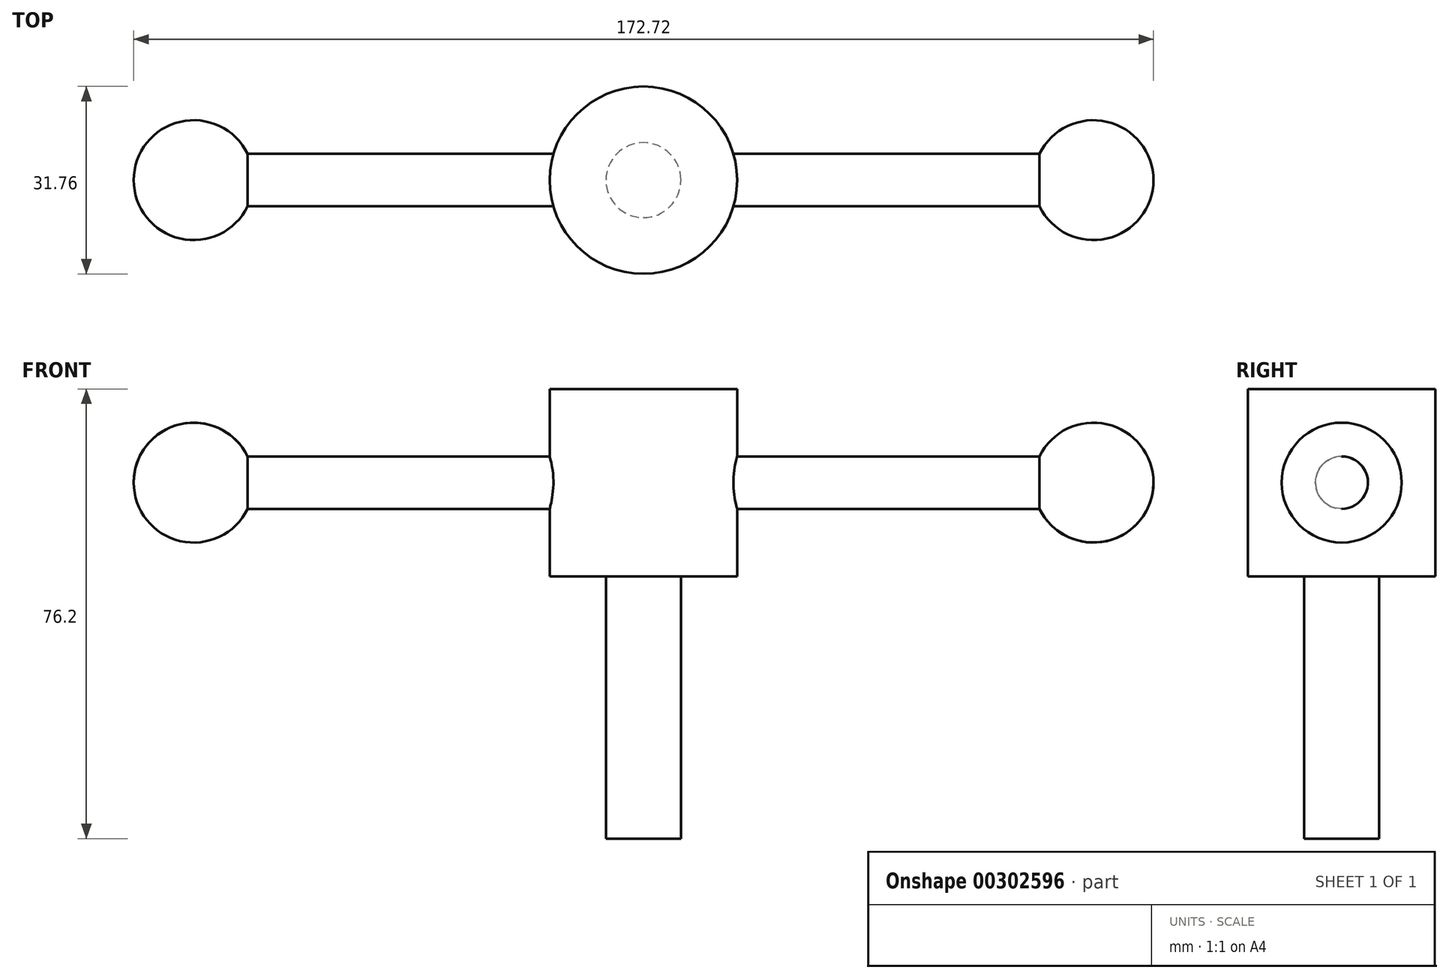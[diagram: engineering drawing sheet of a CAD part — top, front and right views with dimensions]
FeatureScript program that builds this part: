
annotation { "Feature Type Name" : "Feature", "Feature Type Description" : "" }
export const myFeature = defineFeature(function(context is Context, id is Id, definition is map)
    precondition{}
    {
        {
            var Q0;
            Q0=qCreatedBy(makeId("Top.planeOp"),FACE);
            var sketch = newSketch(context, id + "F0", { "sketchPlane" : qUnion([Q0])});
            skCircle(sketch, "E0", {"center": v(0, 0) * mm, "radius": 15.88 * mm});
            skCircle(sketch, "E1", {"center": v(0, 0) * mm, "radius": 6.35 * mm});
            skSolve(sketch);
        }
        {
            var Q0;
            Q0=makeQuery(id+"F0.imprint","IMPRINT",FACE,{"disambiguationData":[TD([[makeQuery(id+"F0.imprint","IMPRINT",EDGE,{"derivedFrom":sQuery(id+"F0.wireOp",EDGE,"E0")}),1.0]])]});
            var Q1;
            Q1=makeQuery(id+"F0.imprint","IMPRINT",FACE,{"disambiguationData":[TD([[makeQuery(id+"F0.imprint","IMPRINT",EDGE,{"derivedFrom":sQuery(id+"F0.wireOp",EDGE,"E1")}),1.0]])]});
            extrude(context, id + "F1", {"entities" : qUnion([Q0, Q1]), "depth" : 31.75 * mm});
        }
        {
            var Q0;
            Q0=makeQuery(id+"F0.imprint","IMPRINT",FACE,{"disambiguationData":[TD([[makeQuery(id+"F0.imprint","IMPRINT",EDGE,{"derivedFrom":sQuery(id+"F0.wireOp",EDGE,"E1")}),1.0]])]});
            extrude(context, id + "F2", {"entities" : qUnion([Q0]), "operationType" : NewBodyOperationType.ADD, "oppositeDirection" : true, "depth" : 44.45 * mm});
        }
        {
            var Q0;
            Q0=qCreatedBy(makeId("Right.planeOp"),FACE);
            var sketch = newSketch(context, id + "F3", { "sketchPlane" : qUnion([Q0])});
            skLineSegment(sketch, "E2", {"start": v(-15.88, 0) * mm, "end": v(-15.88, 31.75) * mm});
            skLineSegment(sketch, "E3", {"start": v(15.88, 31.75) * mm, "end": v(15.88, 0) * mm});
            skCircle(sketch, "E4", {"center": v(0, 15.88) * mm, "radius": 4.45 * mm});
            skSolve(sketch);
        }
        {
            var Q0;
            Q0 = qSketchRegion(id + "F3", true);
            extrude(context, id + "F4", {"entities" : qUnion([Q0]), "operationType" : NewBodyOperationType.ADD, "depth" : 139.7 * mm, "symmetric" : true});
        }
        {
            var Q0;
            Q0=qCreatedBy(makeId("Front.planeOp"),FACE);
            var sketch = newSketch(context, id + "F5", { "sketchPlane" : qUnion([Q0])});
            skArc(sketch, "E5", {"start": v(86.39, 15.88) * mm, "mid": v(76.23, 26.04) * mm, "end": v(66.07, 15.88) * mm});
            skLineSegment(sketch, "E6", {"start": v(15.88, 20.32) * mm, "end": v(66.1, 20.32) * mm});
            skLineSegment(sketch, "E7", {"start": v(66.04, 11.43) * mm, "end": v(15.88, 11.43) * mm});
            skLineSegment(sketch, "E8", {"start": v(76.23, 15.88) * mm, "end": v(66.07, 15.88) * mm});
            skLineSegment(sketch, "E9", {"start": v(66.04, 11.43) * mm, "end": v(66.1, 20.32) * mm});
            skArc(sketch, "E10", {"start": v(-66.01, 15.88) * mm, "mid": v(-76.17, 26.04) * mm, "end": v(-86.33, 15.87) * mm});
            skLineSegment(sketch, "E11", {"start": v(-76.17, 15.88) * mm, "end": v(-66.01, 15.88) * mm, "construction": true});
            skLineSegment(sketch, "E12", {"start": v(-65.98, 20.32) * mm, "end": v(-15.88, 20.32) * mm});
            skLineSegment(sketch, "E13", {"start": v(-15.88, 11.43) * mm, "end": v(-66.04, 11.43) * mm});
            skLineSegment(sketch, "E14", {"start": v(-66.04, 11.43) * mm, "end": v(-65.98, 20.32) * mm});
            skLineSegment(sketch, "E15", {"start": v(-66.01, 15.88) * mm, "end": v(-86.33, 15.88) * mm});
            skLineSegment(sketch, "E16", {"start": v(66.07, 15.88) * mm, "end": v(86.39, 15.88) * mm});
            skLineSegment(sketch, "E17", {"start": v(66.07, 15.88) * mm, "end": v(83.67, 15.88) * mm, "construction": true});
            skLineSegment(sketch, "E18", {"start": v(-69.85, 15.88) * mm, "end": v(-93.59, 15.88) * mm, "construction": true});
            skLineSegment(sketch, "E19", {"start": v(-69.85, 20.32) * mm, "end": v(-15.88, 20.32) * mm});
            skLineSegment(sketch, "E20", {"start": v(-15.88, 11.43) * mm, "end": v(-69.85, 11.43) * mm});
            skLineSegment(sketch, "E21", {"start": v(15.88, 20.32) * mm, "end": v(69.85, 20.32) * mm});
            skLineSegment(sketch, "E22", {"start": v(69.85, 11.43) * mm, "end": v(15.88, 11.43) * mm});
            skLineSegment(sketch, "E23", {"start": v(69.85, 20.32) * mm, "end": v(69.85, 11.43) * mm});
            skLineSegment(sketch, "E24", {"start": v(66.04, 11.43) * mm, "end": v(69.85, 11.43) * mm});
            skLineSegment(sketch, "E25", {"start": v(-69.85, 20.32) * mm, "end": v(-69.85, 11.43) * mm});
            skLineSegment(sketch, "E26", {"start": v(-69.85, 11.43) * mm, "end": v(-66.04, 11.43) * mm});
            skLineSegment(sketch, "E27", {"start": v(-66.04, 11.43) * mm, "end": v(-69.85, 11.43) * mm});
            skSolve(sketch);
        }
        {
            var Q0;
            {var subQ0=sQuery(id+"F5.wireOp",EDGE,"E15");var subQ1=sQuery(id+"F5.wireOp",EDGE,"E10");var subQ2=makeQuery(id+"F5.imprint","INTERSECT",VERTEX,{"derivedFrom":[subQ1,subQ0]});Q0=makeQuery(id+"F5.imprint","IMPRINT",FACE,{"disambiguationData":[TD([[makeQuery(id+"F5.imprint","IMPRINT",EDGE,{"disambiguationData":[TD([[subQ2,1.0]])],"derivedFrom":subQ1}),1.0]])]});}
            var Q1;
            {var subQ0=sQuery(id+"F5.wireOp",EDGE,"E16");var subQ3=makeQuery(id+"F5.imprint","IMPRINT",VERTEX,{"derivedFrom":subQ0});Q1=makeQuery(id+"F5.imprint","IMPRINT",FACE,{"disambiguationData":[TD([[makeQuery(id+"F5.imprint","IMPRINT",EDGE,{"disambiguationData":[TD([[subQ3,1.0]])],"derivedFrom":subQ0}),1.0]])]});}
            var Q2;
            Q2=sQuery(id+"F5.wireOp",EDGE,"E18");
            revolve(context, id + "F6", {"operationType" : NewBodyOperationType.ADD, "entities" : qUnion([Q0, Q1]), "axis" : qUnion([Q2]), "revolveType" : RevolveType.FULL});
        }
    });
